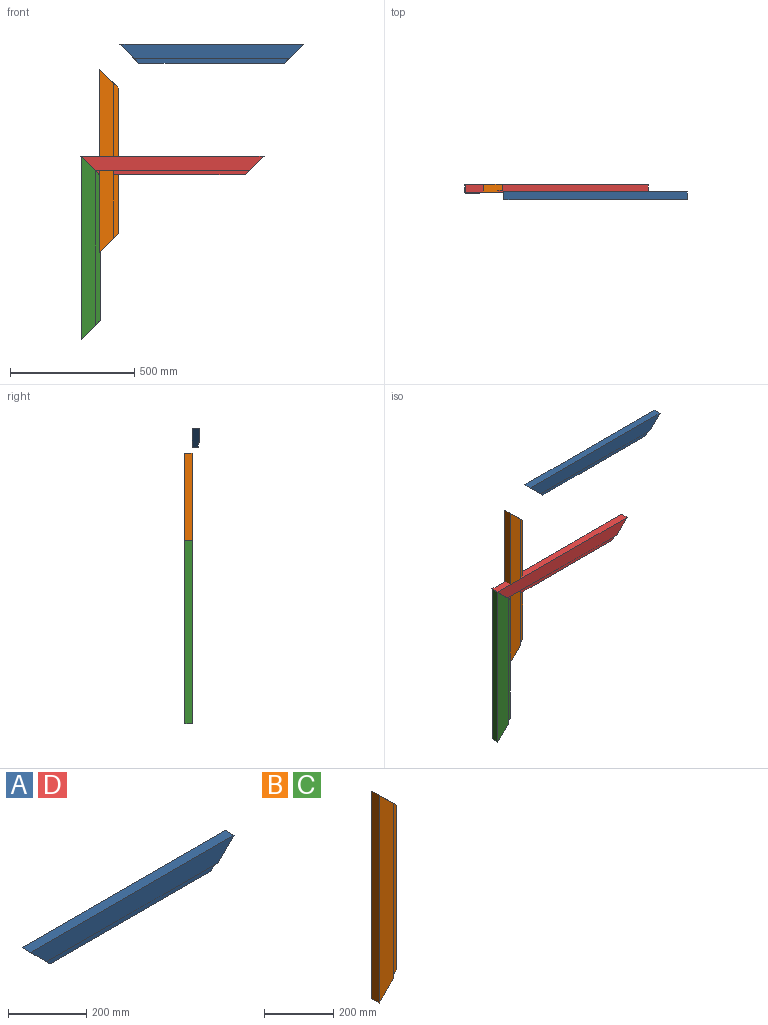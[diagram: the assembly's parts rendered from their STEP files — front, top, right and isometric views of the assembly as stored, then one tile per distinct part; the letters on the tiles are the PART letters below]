
ASSEMBLY  parts=4 mates=1
PART A: 8 faces, bbox 736.6x31.8x76.2 mm
  f0: plane 584.2x25.4mm, normal (0,0,-1), area 14838.7mm2, adj f1,f4,f5,f7
  f1: plane 76.2x76.2mm, normal (0.71,0,-0.71), area 3250.4mm2, adj f0,f2,f3,f5,f6,f7
  f2: plane 736.6x57.15mm, normal (0,-1,0), area 38830.6mm2, adj f1,f3,f4,f6
  f3: plane 736.6x31.75mm, normal (0,0,1), area 23387.1mm2, adj f1,f2,f4,f5
  f4: plane 76.2x76.2mm, normal (-0.71,0,-0.71), area 3250.4mm2, adj f0,f2,f3,f5,f6,f7
  f5: plane 736.6x76.2mm, normal (0,1,0), area 50322.5mm2, adj f0,f1,f3,f4
  f6: plane 622.3x6.35mm, normal (0,0,-1), area 3951.6mm2, adj f1,f2,f4,f7
  f7: plane 622.3x19.05mm, normal (0,-1,0), area 11491.9mm2, adj f0,f1,f4,f6
PART B: 8 faces, bbox 76.2x31.8x736.6 mm
  f0: plane 584.2x25.4mm, normal (1,0,0), area 14838.7mm2, adj f2,f4,f5,f7
  f1: plane 736.6x57.15mm, normal (0,-1,0), area 38830.6mm2, adj f2,f3,f5,f6
  f2: plane 76.2x76.2mm, normal (0.71,0,-0.71), area 3250.4mm2, adj f0,f1,f3,f4,f6,f7
  f3: plane 736.6x31.75mm, normal (-1,0,0), area 23387mm2, adj f1,f2,f4,f5
  f4: plane 736.6x76.2mm, normal (0,1,0), area 50322.5mm2, adj f0,f2,f3,f5
  f5: plane 76.2x76.2mm, normal (0.71,0,0.71), area 3250.4mm2, adj f0,f1,f3,f4,f6,f7
  f6: plane 622.3x6.35mm, normal (1,0,0), area 3951.6mm2, adj f1,f2,f5,f7
  f7: plane 622.3x19.05mm, normal (0,-1,0), area 11491.9mm2, adj f0,f2,f5,f6
PART C: same geometry as B
PART D: same geometry as A
PLACE A at identity
PLACE B t=(0,0,50.8)mm
PLACE C t=(-73.35,-2.97,-299.85)mm
PLACE D t=(-157.58,29.45,-448.92)mm
MATE planar C.f5 <-> D.f4  axis (0.71,0,0.71) through (-286.67,-18.18,400.16)mm
